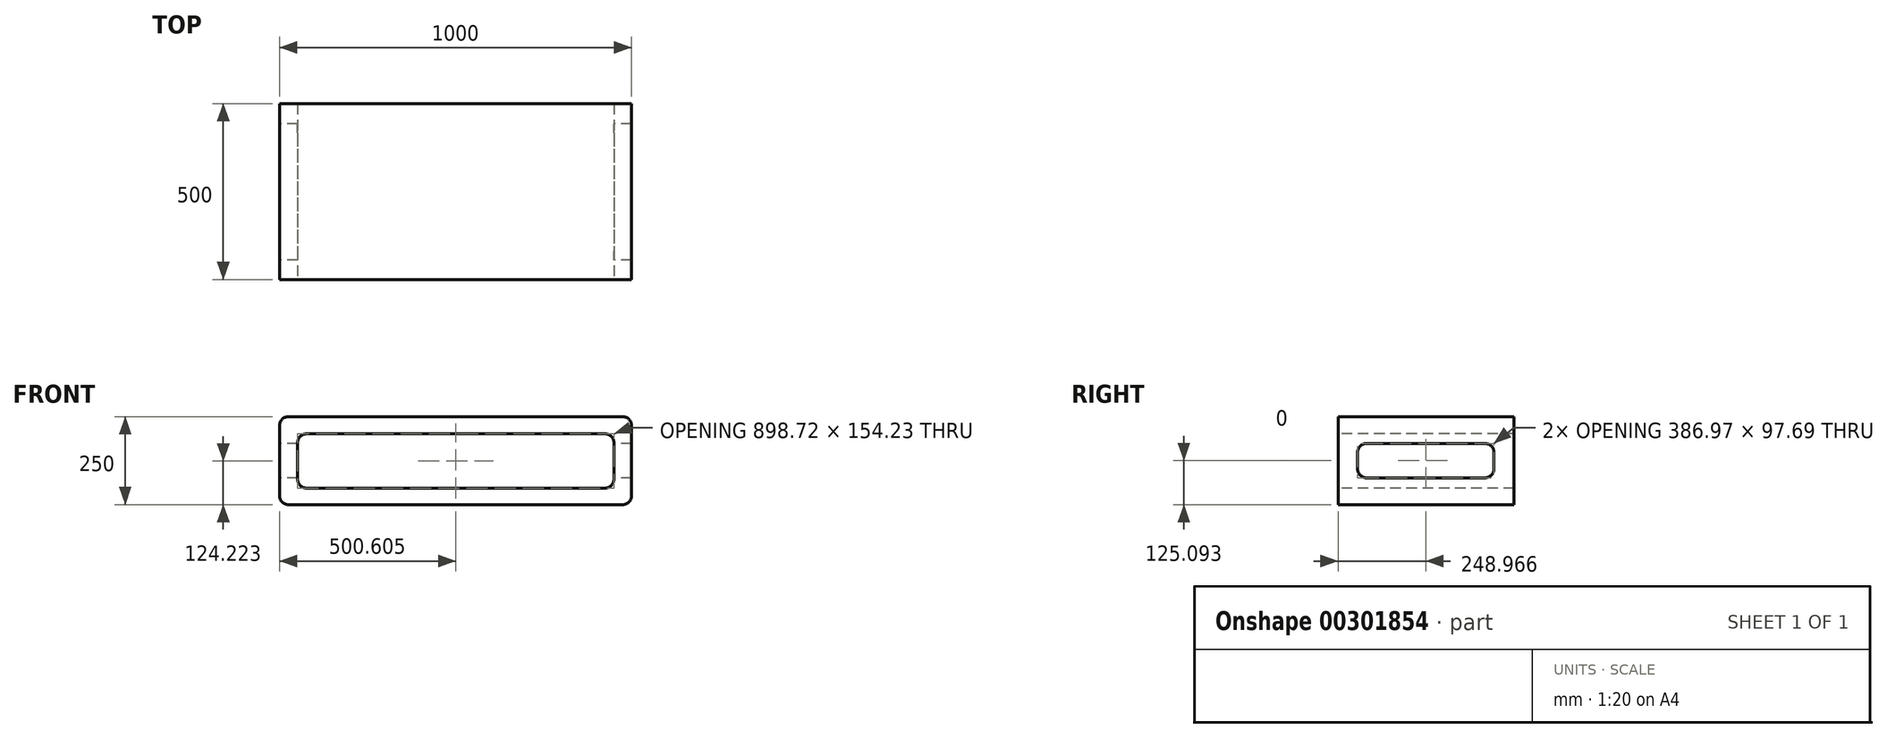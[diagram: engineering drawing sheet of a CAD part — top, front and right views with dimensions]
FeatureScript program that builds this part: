
annotation { "Feature Type Name" : "Feature", "Feature Type Description" : "" }
export const myFeature = defineFeature(function(context is Context, id is Id, definition is map)
    precondition{}
    {
        {
            var Q0;
            Q0=qCreatedBy(makeId("Front.planeOp"),FACE);
            var sketch = newSketch(context, id + "F0", { "sketchPlane" : qUnion([Q0])});
            skLineSegment(sketch, "E0.bottom", {"start": v(1000, 213.46) * mm, "end": v(-1000, 213.46) * mm});
            skLineSegment(sketch, "E0.top", {"start": v(1000, -286.54) * mm, "end": v(-1000, -286.54) * mm});
            skLineSegment(sketch, "E0.left", {"start": v(1000, 213.46) * mm, "end": v(1000, -286.54) * mm});
            skLineSegment(sketch, "E0.right", {"start": v(-1000, 213.46) * mm, "end": v(-1000, -286.54) * mm});
            skPoint(sketch, "E0.middle", {"position": v(0, -36.54) * mm});
            skSolve(sketch);
        }
        {
            var Q0;
            Q0=qSketchRegion(id+"F0",true);
            extrude(context, id + "F1", {"entities" : qUnion([Q0]), "depth" : 1000 * mm});
        }
        {
            var Q0;
            Q0=makeQuery(id+"F1.opExtrude","CAP_FACE",FACE,{"disambiguationData":[OSD([sQuery(id+"F0.wireOp",EDGE,"E0.bottom"),sQuery(id+"F0.wireOp",EDGE,"E0.top"),sQuery(id+"F0.wireOp",EDGE,"E0.left"),sQuery(id+"F0.wireOp",EDGE,"E0.right")])],"isStart":false});
            var sketch = newSketch(context, id + "F2", { "sketchPlane" : qUnion([Q0])});
            skLineSegment(sketch, "E1.bottom", {"start": v(-897.51, 116.14) * mm, "end": v(899.93, 116.14) * mm});
            skLineSegment(sketch, "E1.top", {"start": v(-897.51, -192.33) * mm, "end": v(899.93, -192.33) * mm});
            skLineSegment(sketch, "E1.left", {"start": v(-897.51, 116.14) * mm, "end": v(-897.51, -192.33) * mm});
            skLineSegment(sketch, "E1.right", {"start": v(899.93, 116.14) * mm, "end": v(899.93, -192.33) * mm});
            skSolve(sketch);
        }
        {
            var Q0;
            Q0=makeQuery(id+"F2.imprint","IMPRINT",FACE,{"disambiguationData":[TD([[makeQuery(id+"F2.imprint","IMPRINT",EDGE,{"derivedFrom":sQuery(id+"F2.wireOp",EDGE,"E1.bottom")}),-1.0]])]});
            extrude(context, id + "F3", {"entities" : qUnion([Q0]), "operationType" : NewBodyOperationType.REMOVE, "endBound" : BoundingType.THROUGH_ALL, "oppositeDirection" : true, "depth" : 25 * mm});
        }
        {
            var Q0;
            Q0=makeQuery(id+"F1.opExtrude","SWEPT_EDGE",EDGE,{"disambiguationData":[OSD([sQuery(id+"F0.wireOp",EDGE,"E0.bottom"),sQuery(id+"F0.wireOp",EDGE,"E0.left")])]});
            var Q1;
            Q1=makeQuery(id+"F1.opExtrude","SWEPT_EDGE",EDGE,{"disambiguationData":[OSD([sQuery(id+"F0.wireOp",EDGE,"E0.top"),sQuery(id+"F0.wireOp",EDGE,"E0.left")])]});
            var Q2;
            Q2=makeQuery(id+"F1.opExtrude","SWEPT_EDGE",EDGE,{"disambiguationData":[OSD([sQuery(id+"F0.wireOp",EDGE,"E0.bottom"),sQuery(id+"F0.wireOp",EDGE,"E0.right")])]});
            var Q3;
            Q3=makeQuery(id+"F1.opExtrude","SWEPT_EDGE",EDGE,{"disambiguationData":[OSD([sQuery(id+"F0.wireOp",EDGE,"E0.top"),sQuery(id+"F0.wireOp",EDGE,"E0.right")])]});
            var Q4;
            Q4=makeQuery(id+"F3.boolean.opBoolean","COPY",EDGE,{"derivedFrom":makeQuery(id+"F3.opExtrude","SWEPT_EDGE",EDGE,{"disambiguationData":[OSD([sQuery(id+"F2.wireOp",EDGE,"E1.bottom"),sQuery(id+"F2.wireOp",EDGE,"E1.left")])]})});
            var Q5;
            Q5=makeQuery(id+"F3.boolean.opBoolean","COPY",EDGE,{"derivedFrom":makeQuery(id+"F3.opExtrude","SWEPT_EDGE",EDGE,{"disambiguationData":[OSD([sQuery(id+"F2.wireOp",EDGE,"E1.top"),sQuery(id+"F2.wireOp",EDGE,"E1.left")])]})});
            var Q6;
            Q6=makeQuery(id+"F3.boolean.opBoolean","COPY",EDGE,{"derivedFrom":makeQuery(id+"F3.opExtrude","SWEPT_EDGE",EDGE,{"disambiguationData":[OSD([sQuery(id+"F2.wireOp",EDGE,"E1.bottom"),sQuery(id+"F2.wireOp",EDGE,"E1.right")])]})});
            var Q7;
            Q7=makeQuery(id+"F3.boolean.opBoolean","COPY",EDGE,{"derivedFrom":makeQuery(id+"F3.opExtrude","SWEPT_EDGE",EDGE,{"disambiguationData":[OSD([sQuery(id+"F2.wireOp",EDGE,"E1.top"),sQuery(id+"F2.wireOp",EDGE,"E1.right")])]})});
            fillet(context, id + "F4", {"entities" : qUnion([Q0, Q1, Q2, Q3, Q4, Q5, Q6, Q7]), "radius" : 50 * mm, "tangentPropagation" : true, "allowEdgeOverflow" : false});
        }
        {
            var Q0;
            Q0=makeQuery(id+"F1.opExtrude","SWEPT_FACE",FACE,{"disambiguationData":[OSD([sQuery(id+"F0.wireOp",EDGE,"E0.right")])]});
            var sketch = newSketch(context, id + "F5", { "sketchPlane" : qUnion([Q0])});
            skLineSegment(sketch, "E2.bottom", {"start": v(115.1, 61.33) * mm, "end": v(889.04, 61.33) * mm});
            skLineSegment(sketch, "E2.top", {"start": v(115.1, -134.04) * mm, "end": v(889.04, -134.04) * mm});
            skLineSegment(sketch, "E2.left", {"start": v(115.1, 61.33) * mm, "end": v(115.1, -134.04) * mm});
            skLineSegment(sketch, "E2.right", {"start": v(889.04, 61.33) * mm, "end": v(889.04, -134.04) * mm});
            skSolve(sketch);
        }
        {
            var Q0;
            Q0=makeQuery(id+"F5.imprint","IMPRINT",FACE,{"disambiguationData":[TD([[makeQuery(id+"F5.imprint","IMPRINT",EDGE,{"derivedFrom":sQuery(id+"F5.wireOp",EDGE,"E2.bottom")}),-1.0]])]});
            extrude(context, id + "F6", {"entities" : qUnion([Q0]), "operationType" : NewBodyOperationType.REMOVE, "endBound" : BoundingType.THROUGH_ALL, "oppositeDirection" : true, "depth" : 25 * mm});
        }
        {
            var Q0;
            {var subQ0=sQuery(id+"F5.wireOp",EDGE,"E2.left");var subQ1=sQuery(id+"F5.wireOp",EDGE,"E2.bottom");Q0=makeQuery(id+"F6.boolean.opBoolean","COPY",EDGE,{"disambiguationData":[TD([makeQuery(id+"F1.opExtrude","SWEPT_FACE",FACE,{"disambiguationData":[OSD([sQuery(id+"F0.wireOp",EDGE,"E0.left")])]})])],"derivedFrom":makeQuery(id+"F6.opExtrude","SWEPT_EDGE",EDGE,{"disambiguationData":[OSD([subQ1,subQ0])]})});}
            var Q1;
            {var subQ0=sQuery(id+"F5.wireOp",EDGE,"E2.bottom");var subQ1=sQuery(id+"F5.wireOp",EDGE,"E2.right");Q1=makeQuery(id+"F6.boolean.opBoolean","COPY",EDGE,{"disambiguationData":[TD([makeQuery(id+"F1.opExtrude","SWEPT_FACE",FACE,{"disambiguationData":[OSD([sQuery(id+"F0.wireOp",EDGE,"E0.left")])]})])],"derivedFrom":makeQuery(id+"F6.opExtrude","SWEPT_EDGE",EDGE,{"disambiguationData":[OSD([subQ0,subQ1])]})});}
            var Q2;
            {var subQ0=sQuery(id+"F5.wireOp",EDGE,"E2.left");var subQ1=sQuery(id+"F5.wireOp",EDGE,"E2.top");Q2=makeQuery(id+"F6.boolean.opBoolean","COPY",EDGE,{"disambiguationData":[TD([makeQuery(id+"F1.opExtrude","SWEPT_FACE",FACE,{"disambiguationData":[OSD([sQuery(id+"F0.wireOp",EDGE,"E0.left")])]})])],"derivedFrom":makeQuery(id+"F6.opExtrude","SWEPT_EDGE",EDGE,{"disambiguationData":[OSD([subQ1,subQ0])]})});}
            var Q3;
            {var subQ0=sQuery(id+"F5.wireOp",EDGE,"E2.top");var subQ1=sQuery(id+"F5.wireOp",EDGE,"E2.right");Q3=makeQuery(id+"F6.boolean.opBoolean","COPY",EDGE,{"disambiguationData":[TD([makeQuery(id+"F1.opExtrude","SWEPT_FACE",FACE,{"disambiguationData":[OSD([sQuery(id+"F0.wireOp",EDGE,"E0.left")])]})])],"derivedFrom":makeQuery(id+"F6.opExtrude","SWEPT_EDGE",EDGE,{"disambiguationData":[OSD([subQ0,subQ1])]})});}
            var Q4;
            {var subQ0=sQuery(id+"F5.wireOp",EDGE,"E2.top");var subQ1=sQuery(id+"F5.wireOp",EDGE,"E2.right");Q4=makeQuery(id+"F6.boolean.opBoolean","COPY",EDGE,{"disambiguationData":[TD([makeQuery(id+"F1.opExtrude","SWEPT_FACE",FACE,{"disambiguationData":[OSD([sQuery(id+"F0.wireOp",EDGE,"E0.right")])]})])],"derivedFrom":makeQuery(id+"F6.opExtrude","SWEPT_EDGE",EDGE,{"disambiguationData":[OSD([subQ0,subQ1])]})});}
            var Q5;
            {var subQ0=sQuery(id+"F5.wireOp",EDGE,"E2.bottom");var subQ1=sQuery(id+"F5.wireOp",EDGE,"E2.right");Q5=makeQuery(id+"F6.boolean.opBoolean","COPY",EDGE,{"disambiguationData":[TD([makeQuery(id+"F1.opExtrude","SWEPT_FACE",FACE,{"disambiguationData":[OSD([sQuery(id+"F0.wireOp",EDGE,"E0.right")])]})])],"derivedFrom":makeQuery(id+"F6.opExtrude","SWEPT_EDGE",EDGE,{"disambiguationData":[OSD([subQ0,subQ1])]})});}
            var Q6;
            {var subQ0=sQuery(id+"F5.wireOp",EDGE,"E2.bottom");var subQ1=sQuery(id+"F5.wireOp",EDGE,"E2.left");Q6=makeQuery(id+"F6.boolean.opBoolean","COPY",EDGE,{"disambiguationData":[TD([makeQuery(id+"F1.opExtrude","SWEPT_FACE",FACE,{"disambiguationData":[OSD([sQuery(id+"F0.wireOp",EDGE,"E0.right")])]})])],"derivedFrom":makeQuery(id+"F6.opExtrude","SWEPT_EDGE",EDGE,{"disambiguationData":[OSD([subQ0,subQ1])]})});}
            var Q7;
            {var subQ0=sQuery(id+"F5.wireOp",EDGE,"E2.top");var subQ1=sQuery(id+"F5.wireOp",EDGE,"E2.left");Q7=makeQuery(id+"F6.boolean.opBoolean","COPY",EDGE,{"disambiguationData":[TD([makeQuery(id+"F1.opExtrude","SWEPT_FACE",FACE,{"disambiguationData":[OSD([sQuery(id+"F0.wireOp",EDGE,"E0.right")])]})])],"derivedFrom":makeQuery(id+"F6.opExtrude","SWEPT_EDGE",EDGE,{"disambiguationData":[OSD([subQ0,subQ1])]})});}
            fillet(context, id + "F7", {"entities" : qUnion([Q0, Q1, Q2, Q3, Q4, Q5, Q6, Q7]), "radius" : 50 * mm, "tangentPropagation" : true, "allowEdgeOverflow" : false});
        }
        {
            var Q0;
            Q0=makeQuery(id+"F1.opExtrude","SWEPT_BODY",BODY,{"disambiguationData":[OSD([sQuery(id+"F0.wireOp",EDGE,"E0.bottom"),sQuery(id+"F0.wireOp",EDGE,"E0.top"),sQuery(id+"F0.wireOp",EDGE,"E0.left"),sQuery(id+"F0.wireOp",EDGE,"E0.right")])]});
            var Q1;
            Q1=qCreatedBy(makeId("Origin.pointOp"),VERTEX);
            transform(context, id + "F8", {"entities" : qUnion([Q0]), "transformType" : TransformType.SCALE_UNIFORMLY, "scale" : 0.5, "scalePoint" : qUnion([Q1]), "makeCopy" : false});
        }
    });
